# Revit family: Скамейка чугунная «Квартал» Арт 7161
name_source: partatom
category: Антураж
revit_build: Autodesk Revit 2018 (Build: 20180423_1000(x64)
units: mm (PartAtom-declared; Revit-internal decimal feet)

## family parameters
Всегда вертикально = Да
Источник визуального образа = Геометрия семейства
На основе рабочей плоскости = Нет
Общий = Нет
При загрузке вырезать с полостями = Нет
Точка расчета площади = Нет

## types (3) — shared parameters
URL = https://hobbyka.ru
Артикул товара = Арт. 7161
Высота = 810 мм
Группа модели = Садовые скамейки
Изготовитель = ООО «Хоббика»
Изображение типоразмера = Скамейка чугунная «Квартал» Арт 7161.jpg
Материал изделия = Чугун, дерево
Цвет лавки = Дерево
Цвет опоры = Чугун
Ширина = 660 мм

## per-type parameters (varying)
| type | Версия 0,6 м (кресло) | Версия 1,5 м | Версия 1,8 м | Длина | Описание |
| Версия 0,6 м (кресло) | Да | Нет | Нет | 600 мм | Скамейка чугунная «Квартал». Версия 0,6 м Кресло |
| Версия 1,5 м | Нет | Да | Нет | 1500 мм | Скамейка чугунная «Квартал». Версия 1,5 м |
| Версия 1,8 м | Нет | Нет | Да | 1800 мм | Скамейка чугунная «Квартал». Версия 1,8 м |
